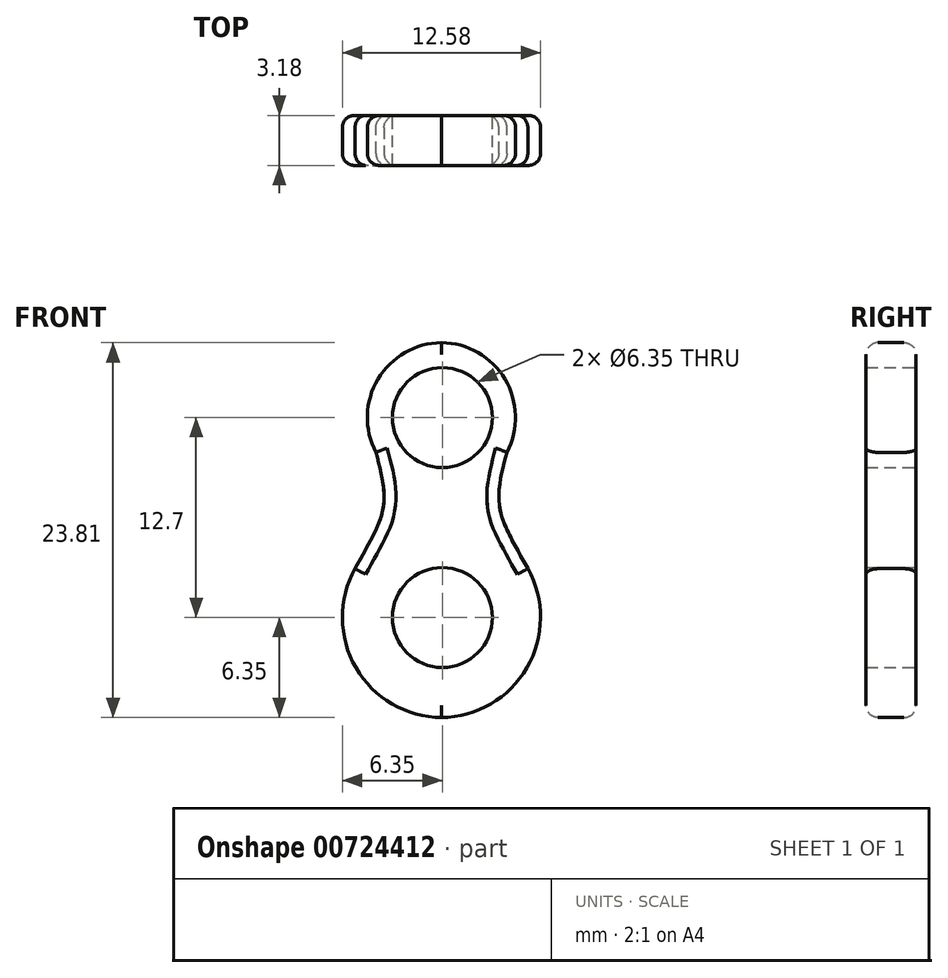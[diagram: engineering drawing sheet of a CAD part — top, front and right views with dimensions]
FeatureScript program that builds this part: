
annotation { "Feature Type Name" : "Feature", "Feature Type Description" : "" }
export const myFeature = defineFeature(function(context is Context, id is Id, definition is map)
    precondition{}
    {
        {
            var Q0;
            Q0=qCreatedBy(makeId("Front.planeOp"),FACE);
            var sketch = newSketch(context, id + "F0", { "sketchPlane" : qUnion([Q0])});
            skFitSpline(sketch, "E0", {"points": [v(-4.22, 10.49) * mm, v(-3.76, 6.94) * mm, v(-5.54, 3.1) * mm], "startDerivative": vector(2.37, -9.09) * mm, "endDerivative": vector(-4.71, -8.72) * mm});
            skArc(sketch, "E1", {"start": v(-0.06, 17.46) * mm, "mid": v(-4.76, 12.7) * mm, "end": v(-0.06, 7.94) * mm});
            skLineSegment(sketch, "E2", {"start": v(-0.06, 17.46) * mm, "end": v(-0.06, 15.87) * mm, "construction": true});
            skLineSegment(sketch, "E3", {"start": v(-0.06, 9.53) * mm, "end": v(-0.06, 3.17) * mm, "construction": true});
            skLineSegment(sketch, "E4", {"start": v(-0.06, 15.87) * mm, "end": v(-0.06, 9.53) * mm, "construction": true});
            skArc(sketch, "E5", {"start": v(-0.06, 15.87) * mm, "mid": v(-3.17, 12.7) * mm, "end": v(-0.06, 9.53) * mm});
            skArc(sketch, "E6", {"start": v(3.17, 12.78) * mm, "mid": v(3.17, 12.79) * mm, "end": v(3.17, 12.8) * mm});
            skArc(sketch, "E7", {"start": v(-0.06, 6.35) * mm, "mid": v(-6.35, 0) * mm, "end": v(-0.06, -6.35) * mm});
            skLineSegment(sketch, "E8", {"start": v(6.35, -0.07) * mm, "end": v(6.35, -0.07) * mm});
            skArc(sketch, "E9", {"start": v(-0.06, 4.76) * mm, "mid": v(-4.76, 0) * mm, "end": v(-0.06, -4.76) * mm});
            skLineSegment(sketch, "E10", {"start": v(-0.06, 3.17) * mm, "end": v(-0.06, -6.35) * mm, "construction": true});
            skLineSegment(sketch, "E11", {"start": v(3.17, 0) * mm, "end": v(3.17, 0) * mm});
            skFitSpline(sketch, "E12.MirrorCS", {"points": [v(4.1, 10.49) * mm, v(3.65, 6.94) * mm, v(5.43, 3.1) * mm], "startDerivative": vector(-2.37, -9.09) * mm, "endDerivative": vector(4.71, -8.72) * mm});
            skArc(sketch, "E13.MirrorCS", {"start": v(-0.06, 15.87) * mm, "mid": v(3.06, 12.7) * mm, "end": v(-0.06, 9.53) * mm});
            skArc(sketch, "E14.MirrorCS", {"start": v(-0.06, 17.46) * mm, "mid": v(4.65, 12.7) * mm, "end": v(-0.06, 7.94) * mm});
            skArc(sketch, "E15.MirrorCS", {"start": v(-0.06, 6.35) * mm, "mid": v(6.23, 0) * mm, "end": v(-0.06, -6.35) * mm});
            skArc(sketch, "E16.MirrorCS", {"start": v(-0.06, 4.76) * mm, "mid": v(4.65, 0) * mm, "end": v(-0.06, -4.76) * mm});
            skCircle(sketch, "E17", {"center": v(0, 0) * mm, "radius": 3.18 * mm});
            skSolve(sketch);
        }
        {
            var Q0;
            {var subQ1=sQuery(id+"F0.wireOp",EDGE,"E0");Q0=makeQuery(id+"F0.imprint","IMPRINT",FACE,{"disambiguationData":[TD([[makeQuery(id+"F0.imprint","IMPRINT",EDGE,{"derivedFrom":subQ1}),1.0]])]});}
            var Q1;
            Q1=makeQuery(id+"F0.imprint","IMPRINT",FACE,{"disambiguationData":[TD([[makeQuery(id+"F0.imprint","IMPRINT",EDGE,{"derivedFrom":sQuery(id+"F0.wireOp",EDGE,"E17")}),1.0]])]});
            var Q2;
            Q2=makeQuery(id+"F0.imprint","IMPRINT",FACE,{"disambiguationData":[TD([[makeQuery(id+"F0.imprint","IMPRINT",EDGE,{"derivedFrom":sQuery(id+"F0.wireOp",EDGE,"E9")}),-1.0]])]});
            var Q3;
            Q3=makeQuery(id+"F0.imprint","IMPRINT",FACE,{"disambiguationData":[TD([[makeQuery(id+"F0.imprint","IMPRINT",EDGE,{"derivedFrom":sQuery(id+"F0.wireOp",EDGE,"E5")}),1.0]])]});
            var Q4;
            Q4=makeQuery(id+"F0.imprint","IMPRINT",FACE,{"disambiguationData":[TD([[makeQuery(id+"F0.imprint","IMPRINT",EDGE,{"derivedFrom":sQuery(id+"F0.wireOp",EDGE,"E9")}),1.0]])]});
            extrude(context, id + "F1", {"entities" : qUnion([Q0, Q1, Q2, Q3, Q4]), "depth" : 3.17 * mm, "offsetDistance" : 25.4 * mm});
        }
        {
            var Q0;
            Q0=makeQuery(id+"F1.opExtrude","CAP_FACE",FACE,{"disambiguationData":[OSD([sQuery(id+"F0.wireOp",EDGE,"E0"),sQuery(id+"F0.wireOp",EDGE,"E1"),sQuery(id+"F0.wireOp",EDGE,"E7"),sQuery(id+"F0.wireOp",EDGE,"E12.MirrorCS"),sQuery(id+"F0.wireOp",EDGE,"E14.MirrorCS"),sQuery(id+"F0.wireOp",EDGE,"E15.MirrorCS")])],"isStart":true});
            var sketch = newSketch(context, id + "F2", { "sketchPlane" : qUnion([Q0])});
            skCircle(sketch, "E18", {"center": v(0, 0) * mm, "radius": 3.18 * mm});
            skSolve(sketch);
        }
        {
            var Q0;
            Q0=makeQuery(id+"F2.imprint","IMPRINT",FACE,{"disambiguationData":[TD([[makeQuery(id+"F2.imprint","IMPRINT",EDGE,{"derivedFrom":sQuery(id+"F2.wireOp",EDGE,"E18")}),1.0]])]});
            extrude(context, id + "F3", {"entities" : qUnion([Q0]), "operationType" : NewBodyOperationType.REMOVE, "oppositeDirection" : true, "depth" : 6.35 * mm, "offsetDistance" : 25.4 * mm});
        }
        {
            var Q0;
            Q0=makeQuery(id+"F1.opExtrude","CAP_FACE",FACE,{"disambiguationData":[OSD([sQuery(id+"F0.wireOp",EDGE,"E0"),sQuery(id+"F0.wireOp",EDGE,"E1"),sQuery(id+"F0.wireOp",EDGE,"E7"),sQuery(id+"F0.wireOp",EDGE,"E12.MirrorCS"),sQuery(id+"F0.wireOp",EDGE,"E14.MirrorCS"),sQuery(id+"F0.wireOp",EDGE,"E15.MirrorCS")])],"isStart":true});
            var sketch = newSketch(context, id + "F4", { "sketchPlane" : qUnion([Q0])});
            skCircle(sketch, "E19", {"center": v(0, 12.7) * mm, "radius": 3.18 * mm});
            skSolve(sketch);
        }
        {
            var Q0;
            Q0=makeQuery(id+"F4.imprint","IMPRINT",FACE,{"disambiguationData":[TD([[makeQuery(id+"F4.imprint","IMPRINT",EDGE,{"derivedFrom":sQuery(id+"F4.wireOp",EDGE,"E19")}),1.0]])]});
            extrude(context, id + "F5", {"entities" : qUnion([Q0]), "operationType" : NewBodyOperationType.REMOVE, "oppositeDirection" : true, "depth" : 25.4 * mm, "offsetDistance" : 25.4 * mm});
        }
        {
            var Q0;
            Q0=makeQuery(id+"F1.opExtrude","CAP_EDGE",EDGE,{"disambiguationData":[OSD([sQuery(id+"F0.wireOp",EDGE,"E14.MirrorCS")])],"isStart":true});
            var Q1;
            Q1=makeQuery(id+"F1.opExtrude","CAP_EDGE",EDGE,{"disambiguationData":[OSD([sQuery(id+"F0.wireOp",EDGE,"E1")])],"isStart":true});
            var Q2;
            Q2=makeQuery(id+"F1.opExtrude","CAP_EDGE",EDGE,{"disambiguationData":[OSD([sQuery(id+"F0.wireOp",EDGE,"E0")])],"isStart":true});
            var Q3;
            Q3=makeQuery(id+"F1.opExtrude","CAP_EDGE",EDGE,{"disambiguationData":[OSD([sQuery(id+"F0.wireOp",EDGE,"E7")])],"isStart":true});
            var Q4;
            Q4=makeQuery(id+"F1.opExtrude","CAP_EDGE",EDGE,{"disambiguationData":[OSD([sQuery(id+"F0.wireOp",EDGE,"E15.MirrorCS")])],"isStart":true});
            var Q5;
            Q5=makeQuery(id+"F1.opExtrude","CAP_EDGE",EDGE,{"disambiguationData":[OSD([sQuery(id+"F0.wireOp",EDGE,"E12.MirrorCS")])],"isStart":true});
            fillet(context, id + "F6", {"entities" : qUnion([Q0, Q1, Q2, Q3, Q4, Q5]), "radius" : 0.76 * mm, "tangentPropagation" : true, "allowEdgeOverflow" : false});
        }
        {
            var Q0;
            Q0=makeQuery(id+"F1.opExtrude","CAP_EDGE",EDGE,{"disambiguationData":[OSD([sQuery(id+"F0.wireOp",EDGE,"E0")])],"isStart":false});
            var Q1;
            Q1=makeQuery(id+"F1.opExtrude","CAP_EDGE",EDGE,{"disambiguationData":[OSD([sQuery(id+"F0.wireOp",EDGE,"E1")])],"isStart":false});
            var Q2;
            Q2=makeQuery(id+"F1.opExtrude","CAP_EDGE",EDGE,{"disambiguationData":[OSD([sQuery(id+"F0.wireOp",EDGE,"E7")])],"isStart":false});
            var Q3;
            Q3=makeQuery(id+"F1.opExtrude","CAP_EDGE",EDGE,{"disambiguationData":[OSD([sQuery(id+"F0.wireOp",EDGE,"E15.MirrorCS")])],"isStart":false});
            var Q4;
            Q4=makeQuery(id+"F1.opExtrude","CAP_EDGE",EDGE,{"disambiguationData":[OSD([sQuery(id+"F0.wireOp",EDGE,"E12.MirrorCS")])],"isStart":false});
            var Q5;
            Q5=makeQuery(id+"F1.opExtrude","CAP_EDGE",EDGE,{"disambiguationData":[OSD([sQuery(id+"F0.wireOp",EDGE,"E14.MirrorCS")])],"isStart":false});
            fillet(context, id + "F7", {"entities" : qUnion([Q0, Q1, Q2, Q3, Q4, Q5]), "radius" : 0.76 * mm, "tangentPropagation" : true, "allowEdgeOverflow" : false});
        }
    });
